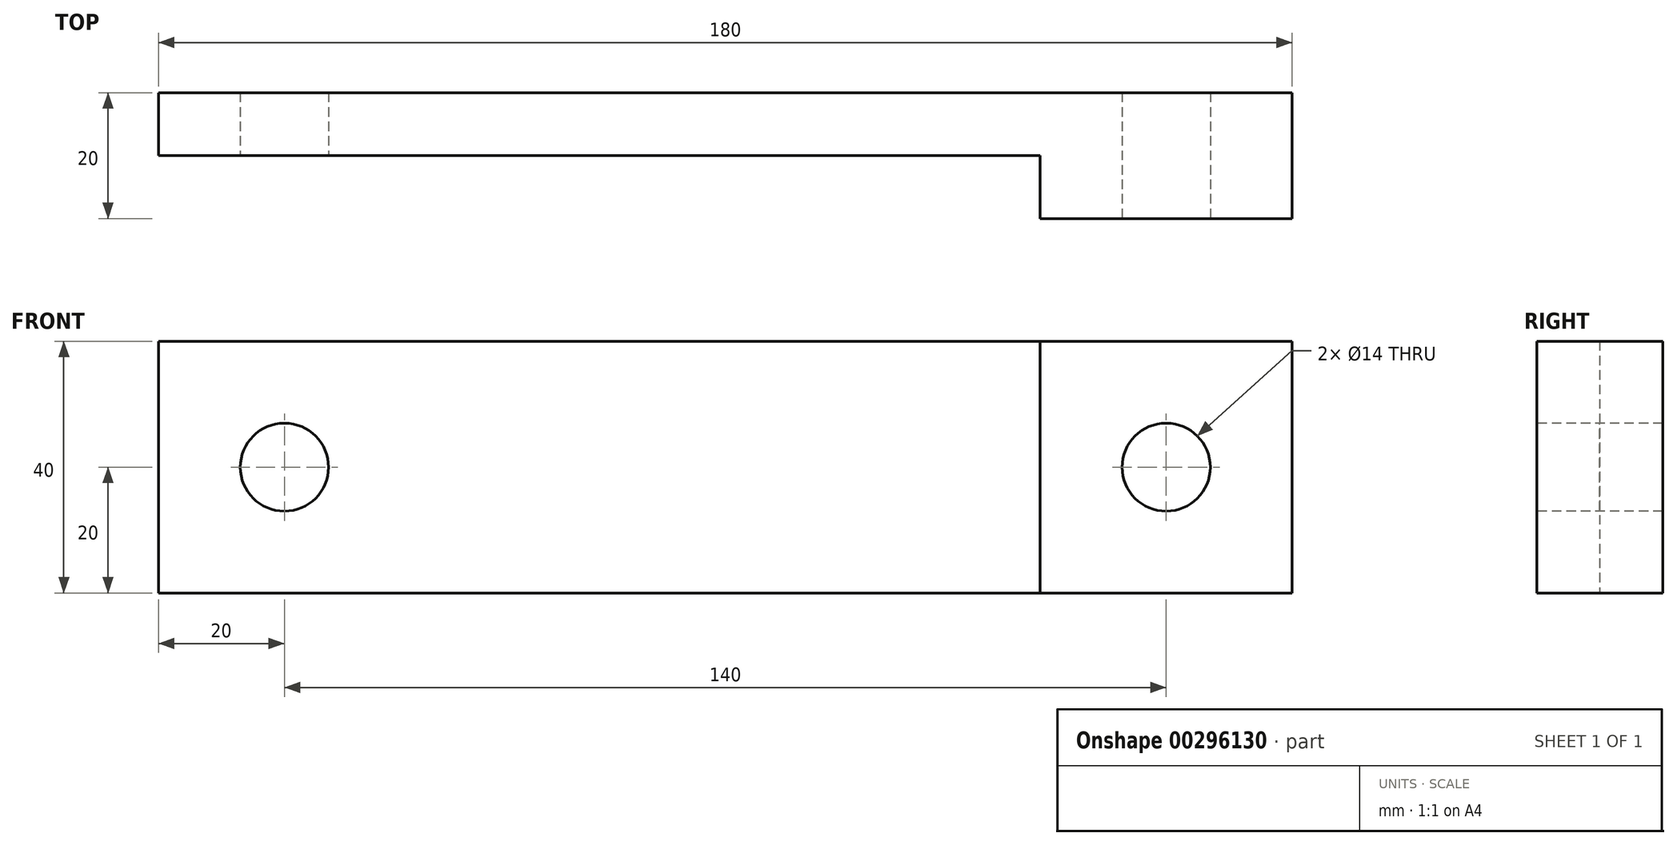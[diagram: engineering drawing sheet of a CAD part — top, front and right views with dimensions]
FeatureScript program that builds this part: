
annotation { "Feature Type Name" : "Feature", "Feature Type Description" : "" }
export const myFeature = defineFeature(function(context is Context, id is Id, definition is map)
    precondition{}
    {
        {
            var Q0;
            Q0=qCreatedBy(makeId("Right.planeOp"),FACE);
            var sketch = newSketch(context, id + "F0", { "sketchPlane" : qUnion([Q0])});
            skLineSegment(sketch, "E0.bottom", {"start": v(5, 20) * mm, "end": v(-5, 20) * mm});
            skLineSegment(sketch, "E0.top", {"start": v(5, -20) * mm, "end": v(-5, -20) * mm});
            skLineSegment(sketch, "E0.left", {"start": v(5, 20) * mm, "end": v(5, -20) * mm});
            skLineSegment(sketch, "E0.right", {"start": v(-5, 20) * mm, "end": v(-5, -20) * mm});
            skPoint(sketch, "E0.middle", {"position": v(0, 0) * mm});
            skSolve(sketch);
        }
        {
            var Q0;
            Q0=makeQuery(id+"F0.imprint","IMPRINT",FACE,{"disambiguationData":[TD([[makeQuery(id+"F0.imprint","IMPRINT",EDGE,{"derivedFrom":sQuery(id+"F0.wireOp",EDGE,"E0.bottom")}),1.0]])]});
            extrude(context, id + "F1", {"entities" : qUnion([Q0]), "oppositeDirection" : true, "depth" : 180 * mm});
        }
        {
            var Q0;
            Q0=makeQuery(id+"F1.opExtrude","SWEPT_FACE",FACE,{"disambiguationData":[OSD([sQuery(id+"F0.wireOp",EDGE,"E0.right")])]});
            var sketch = newSketch(context, id + "F2", { "sketchPlane" : qUnion([Q0])});
            skLineSegment(sketch, "E1", {"start": v(-180, 0) * mm, "end": v(0, 0) * mm, "construction": true});
            skCircle(sketch, "E2", {"center": v(-160, 0) * mm, "radius": 7 * mm});
            skCircle(sketch, "E3", {"center": v(-20, 0) * mm, "radius": 7 * mm});
            skSolve(sketch);
        }
        {
            var Q0;
            Q0=makeQuery(id+"F2.imprint","IMPRINT",FACE,{"disambiguationData":[TD([[makeQuery(id+"F2.imprint","IMPRINT",EDGE,{"derivedFrom":sQuery(id+"F2.wireOp",EDGE,"E2")}),1.0]])]});
            var Q1;
            Q1=makeQuery(id+"F2.imprint","IMPRINT",FACE,{"disambiguationData":[TD([[makeQuery(id+"F2.imprint","IMPRINT",EDGE,{"derivedFrom":sQuery(id+"F2.wireOp",EDGE,"E3")}),1.0]])]});
            extrude(context, id + "F3", {"entities" : qUnion([Q0, Q1]), "operationType" : NewBodyOperationType.REMOVE, "endBound" : BoundingType.THROUGH_ALL, "oppositeDirection" : true, "depth" : 25 * mm});
        }
        {
            var Q0;
            Q0=makeQuery(id+"F1.opExtrude","SWEPT_FACE",FACE,{"disambiguationData":[OSD([sQuery(id+"F0.wireOp",EDGE,"E0.right")])]});
            var sketch = newSketch(context, id + "F4", { "sketchPlane" : qUnion([Q0])});
            skLineSegment(sketch, "E4.bottom", {"start": v(0, 20) * mm, "end": v(-40, 20) * mm});
            skLineSegment(sketch, "E4.top", {"start": v(0, -20) * mm, "end": v(-40, -20) * mm});
            skLineSegment(sketch, "E4.left", {"start": v(0, 20) * mm, "end": v(0, -20) * mm});
            skLineSegment(sketch, "E4.right", {"start": v(-40, 20) * mm, "end": v(-40, -20) * mm});
            skSolve(sketch);
        }
        {
            var Q0;
            Q0=makeQuery(id+"F4.imprint","IMPRINT",FACE,{"disambiguationData":[TD([[makeQuery(id+"F4.imprint","IMPRINT",EDGE,{"derivedFrom":sQuery(id+"F4.wireOp",EDGE,"E4.bottom")}),-1.0]])]});
            extrude(context, id + "F5", {"entities" : qUnion([Q0]), "operationType" : NewBodyOperationType.ADD, "depth" : 10 * mm});
        }
    });
